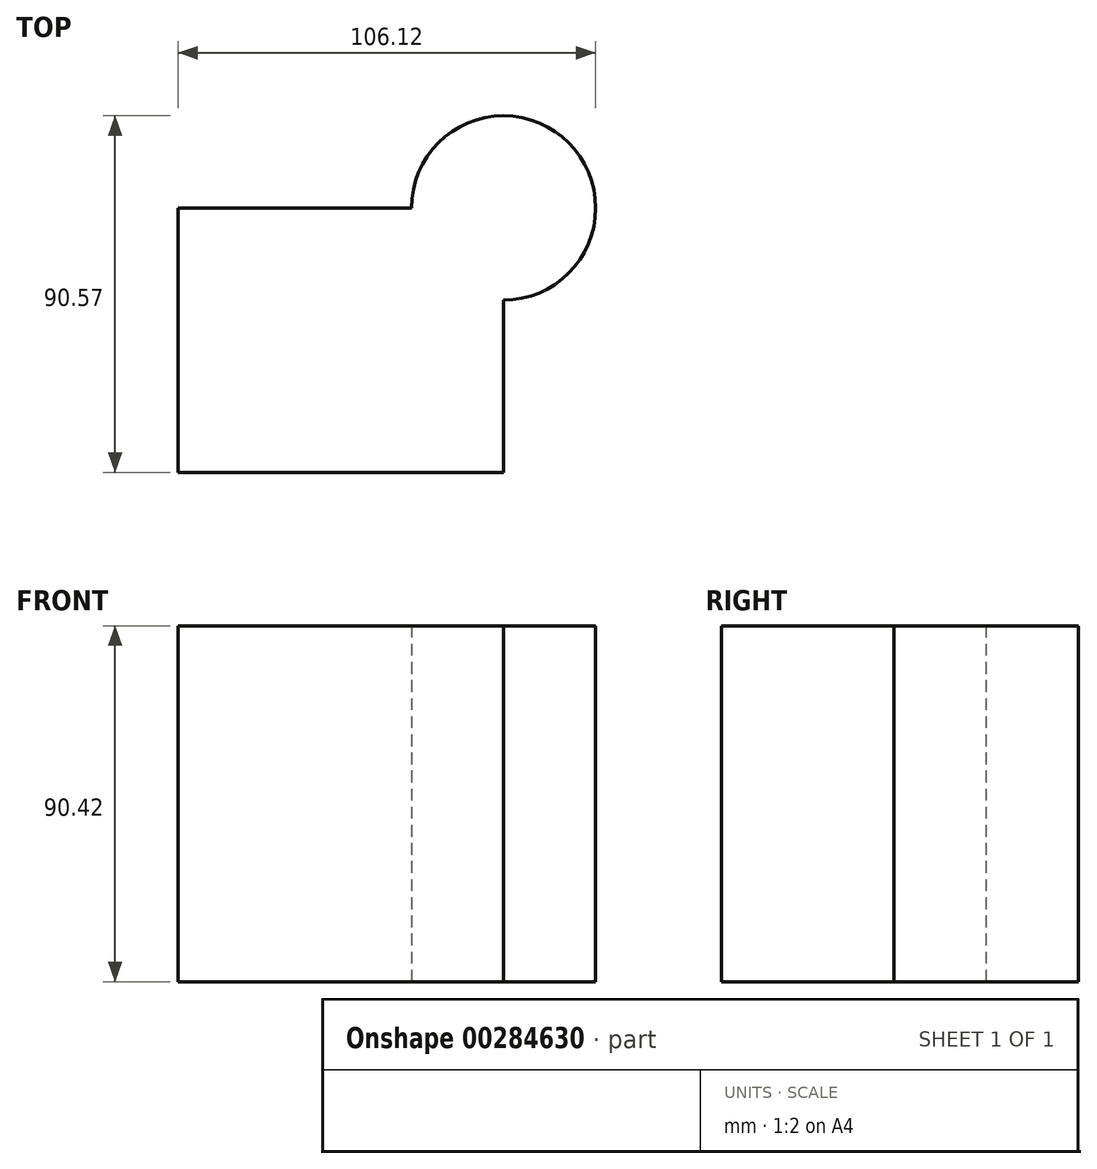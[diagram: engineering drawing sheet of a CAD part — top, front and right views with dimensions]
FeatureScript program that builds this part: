
annotation { "Feature Type Name" : "Feature", "Feature Type Description" : "" }
export const myFeature = defineFeature(function(context is Context, id is Id, definition is map)
    precondition{}
    {
        {
            var Q0;
            Q0=qCreatedBy(makeId("Top.planeOp"),FACE);
            var sketch = newSketch(context, id + "F0", { "sketchPlane" : qUnion([Q0])});
            skLineSegment(sketch, "E0.bottom", {"start": v(-43.86, 11.55) * mm, "end": v(15.45, 11.55) * mm});
            skLineSegment(sketch, "E0.top", {"start": v(-43.86, -55.61) * mm, "end": v(38.85, -55.61) * mm});
            skLineSegment(sketch, "E0.left", {"start": v(-43.86, 11.55) * mm, "end": v(-43.86, -55.61) * mm});
            skLineSegment(sketch, "E0.right", {"start": v(38.85, -11.85) * mm, "end": v(38.85, -55.61) * mm});
            skArc(sketch, "E1", {"start": v(38.85, -11.85) * mm, "mid": v(55.4, 28.1) * mm, "end": v(15.45, 11.55) * mm});
            skSolve(sketch);
        }
        {
            var Q0;
            Q0=makeQuery(id+"F0.imprint","IMPRINT",FACE,{"disambiguationData":[TD([[makeQuery(id+"F0.imprint","IMPRINT",EDGE,{"derivedFrom":sQuery(id+"F0.wireOp",EDGE,"E0.bottom")}),-1.0]])]});
            extrude(context, id + "F1", {"entities" : qUnion([Q0]), "depth" : 90.42 * mm});
        }
    });
